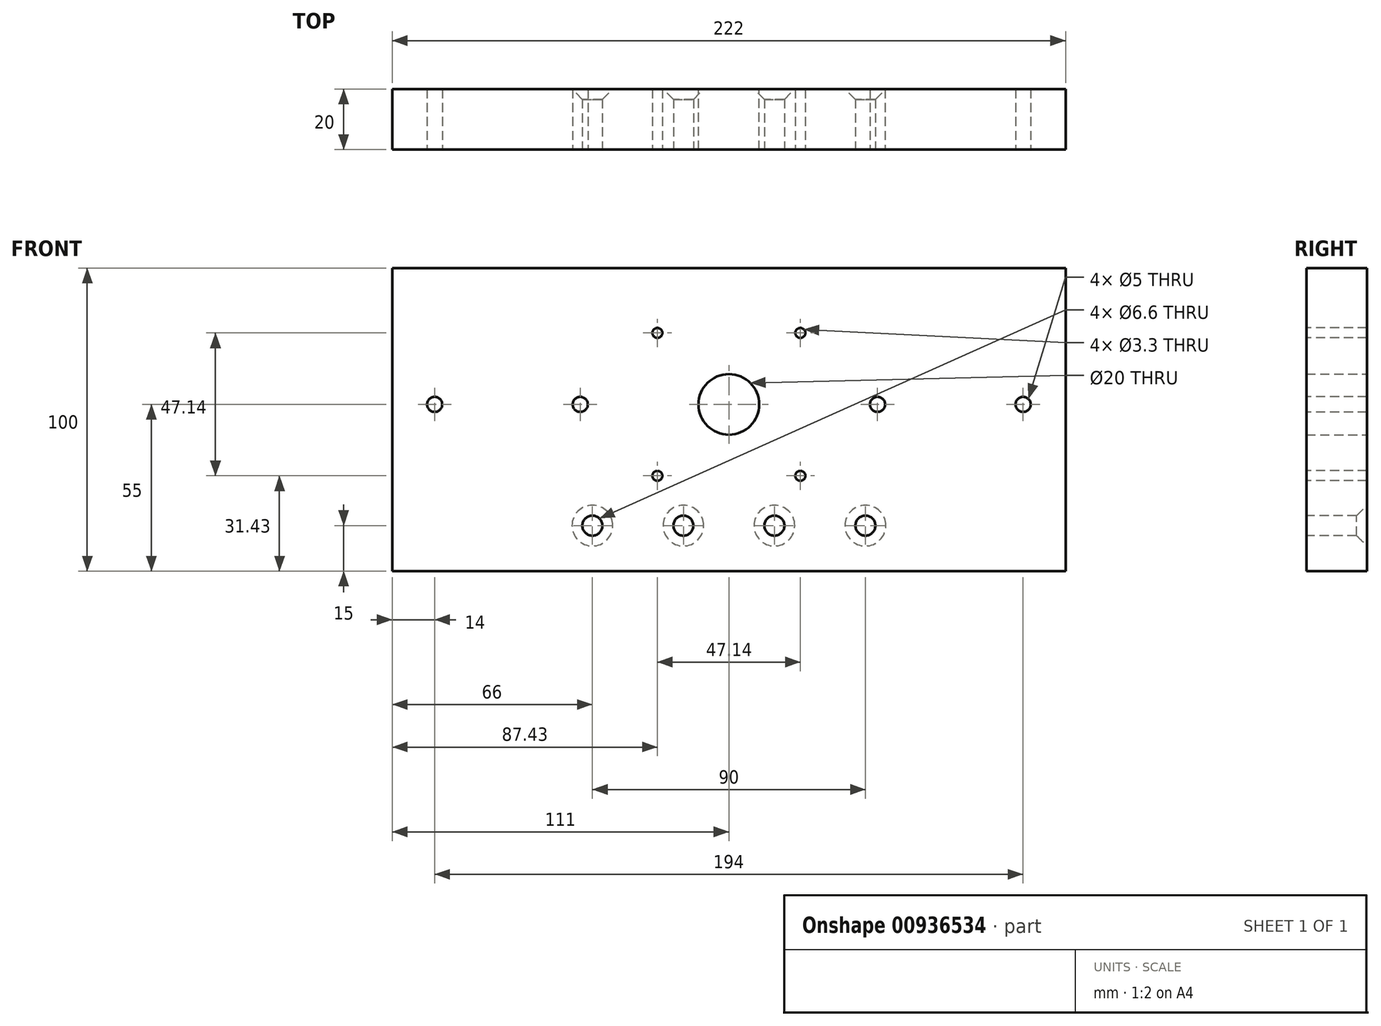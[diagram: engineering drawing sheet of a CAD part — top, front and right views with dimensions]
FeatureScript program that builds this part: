
annotation { "Feature Type Name" : "Feature", "Feature Type Description" : "" }
export const myFeature = defineFeature(function(context is Context, id is Id, definition is map)
    precondition{}
    {
        {
            var Q0;
            Q0=qCreatedBy(makeId("Front.planeOp"),FACE);
            var sketch = newSketch(context, id + "F0", { "sketchPlane" : qUnion([Q0])});
            skLineSegment(sketch, "E0.bottom", {"start": v(-111, -50) * mm, "end": v(111, -50) * mm});
            skLineSegment(sketch, "E0.top", {"start": v(-111, 50) * mm, "end": v(111, 50) * mm});
            skLineSegment(sketch, "E0.left", {"start": v(-111, -50) * mm, "end": v(-111, 50) * mm});
            skLineSegment(sketch, "E0.right", {"start": v(111, -50) * mm, "end": v(111, 50) * mm});
            skPoint(sketch, "E0.middle", {"position": v(0, 0) * mm});
            skLineSegment(sketch, "E1", {"start": v(-111, 5) * mm, "end": v(111, 5) * mm, "construction": true});
            skLineSegment(sketch, "E2", {"start": v(-73, 41.24) * mm, "end": v(-73, 0) * mm, "construction": true});
            skLineSegment(sketch, "E3.MirrorCS", {"start": v(73, 41.24) * mm, "end": v(73, 0) * mm, "construction": true});
            skLineSegment(sketch, "E4", {"start": v(-111, -20) * mm, "end": v(111, -20) * mm, "construction": true});
            skLineSegment(sketch, "E5", {"start": v(-97.11, -35) * mm, "end": v(93.84, -35) * mm, "construction": true});
            skPoint(sketch, "E6", {"position": v(-97, 5) * mm});
            skPoint(sketch, "E7.MirrorP", {"position": v(-49, 5) * mm});
            skPoint(sketch, "E8.MirrorP", {"position": v(49, 5) * mm});
            skPoint(sketch, "E9.MirrorP", {"position": v(97, 5) * mm});
            skPoint(sketch, "E10", {"position": v(-15, -35) * mm});
            skPoint(sketch, "E11", {"position": v(-45, -35) * mm});
            skPoint(sketch, "E12.MirrorP", {"position": v(15, -35) * mm});
            skPoint(sketch, "E13.MirrorP", {"position": v(45, -35) * mm});
            skCircle(sketch, "E14", {"center": v(0, 5) * mm, "radius": 10 * mm});
            skLineSegment(sketch, "E15.bottom", {"start": v(23.57, 28.57) * mm, "end": v(-23.57, 28.57) * mm, "construction": true});
            skLineSegment(sketch, "E15.top", {"start": v(23.57, -18.57) * mm, "end": v(-23.57, -18.57) * mm, "construction": true});
            skLineSegment(sketch, "E15.left", {"start": v(23.57, 28.57) * mm, "end": v(23.57, -18.57) * mm, "construction": true});
            skLineSegment(sketch, "E15.right", {"start": v(-23.57, 28.57) * mm, "end": v(-23.57, -18.57) * mm, "construction": true});
            skSolve(sketch);
        }
        {
            var Q0;
            Q0=makeQuery(id+"F0.imprint","IMPRINT",FACE,{"disambiguationData":[TD([[makeQuery(id+"F0.imprint","IMPRINT",EDGE,{"derivedFrom":sQuery(id+"F0.wireOp",EDGE,"E0.bottom")}),1.0]])]});
            extrude(context, id + "F1", {"entities" : qUnion([Q0]), "depth" : 20 * mm, "offsetDistance" : 25 * mm});
        }
        {
            var Q0;
            Q0=sQuery(id+"F0.wireOp",VERTEX,"E8.MirrorP");
            var Q1;
            Q1=sQuery(id+"F0.wireOp",VERTEX,"E9.MirrorP");
            var Q2;
            Q2=sQuery(id+"F0.wireOp",VERTEX,"E7.MirrorP");
            var Q3;
            Q3=sQuery(id+"F0.wireOp",VERTEX,"E6");
            var Q4;
            Q4=makeQuery(id+"F1.opExtrude","SWEPT_BODY",BODY,{"disambiguationData":[OSD([sQuery(id+"F0.wireOp",EDGE,"E0.bottom"),sQuery(id+"F0.wireOp",EDGE,"E0.top"),sQuery(id+"F0.wireOp",EDGE,"E0.left"),sQuery(id+"F0.wireOp",EDGE,"E0.right")])]});
            hole(context, id + "F2", {"style" : HoleStyle.SIMPLE, "endStyle" : HoleEndStyle.THROUGH, "oppositeDirection" : true, "standardTappedOrClearance" : lookupTablePath({ "standard" : "ISO", "engagement" : "75%", "pitch" : "1 mm", "size" : "M6", "type" : "Tapped" }), "standardBlindInLast" : lookupTablePath({ "standard" : "ISO", "engagement" : "75%", "pitch" : "1 mm", "size" : "M6", "type" : "Tapped" }), "holeDiameter" : 5 * mm, "majorDiameter" : 6 * mm, "showTappedDepth" : true, "tappedDepth" : 12 * mm, "tapClearance" : 3, "locations" : qUnion([Q0, Q1, Q2, Q3]), "scope" : qUnion([Q4]), "startStyle" : HoleStartStyle.PART});
        }
        {
            var Q0;
            Q0=sQuery(id+"F0.wireOp",VERTEX,"E11");
            var Q1;
            Q1=sQuery(id+"F0.wireOp",VERTEX,"E10");
            var Q2;
            Q2=sQuery(id+"F0.wireOp",VERTEX,"E12.MirrorP");
            var Q3;
            Q3=sQuery(id+"F0.wireOp",VERTEX,"E13.MirrorP");
            var Q4;
            Q4=makeQuery(id+"F1.opExtrude","SWEPT_BODY",BODY,{"disambiguationData":[OSD([sQuery(id+"F0.wireOp",EDGE,"E0.bottom"),sQuery(id+"F0.wireOp",EDGE,"E0.top"),sQuery(id+"F0.wireOp",EDGE,"E0.left"),sQuery(id+"F0.wireOp",EDGE,"E0.right")])]});
            hole(context, id + "F3", {"style" : HoleStyle.C_SINK, "endStyle" : HoleEndStyle.THROUGH, "oppositeDirection" : true, "standardTappedOrClearance" : lookupTablePath({ "fit" : "Normal", "standard" : "ISO", "size" : "M6", "type" : "Clearance" }), "standardBlindInLast" : lookupTablePath({ "fit" : "Standard", "standard" : "ISO", "size" : "M6", "type" : "Clearance" }), "holeDiameter" : 6.6 * mm, "cSinkDiameter" : 13.44 * mm, "cSinkAngle" : 90 * degree, "majorDiameter" : 6 * mm, "tappedDepth" : 12 * mm, "tapClearance" : 3, "locations" : qUnion([Q0, Q1, Q2, Q3]), "scope" : qUnion([Q4]), "startStyle" : HoleStartStyle.PART});
        }
        {
            var Q0;
            Q0=sQuery(id+"F0.wireOp",VERTEX,"E15.bottom.start");
            var Q1;
            Q1=sQuery(id+"F0.wireOp",VERTEX,"E15.bottom.end");
            var Q2;
            Q2=sQuery(id+"F0.wireOp",VERTEX,"E15.top.start");
            var Q3;
            Q3=sQuery(id+"F0.wireOp",VERTEX,"E15.top.end");
            var Q4;
            Q4=makeQuery(id+"F1.opExtrude","SWEPT_BODY",BODY,{"disambiguationData":[OSD([sQuery(id+"F0.wireOp",EDGE,"E0.bottom"),sQuery(id+"F0.wireOp",EDGE,"E0.top"),sQuery(id+"F0.wireOp",EDGE,"E0.left"),sQuery(id+"F0.wireOp",EDGE,"E0.right"),sQuery(id+"F0.wireOp",EDGE,"E14")])]});
            hole(context, id + "F4", {"style" : HoleStyle.SIMPLE, "endStyle" : HoleEndStyle.THROUGH, "oppositeDirection" : true, "standardTappedOrClearance" : lookupTablePath({ "standard" : "ISO", "engagement" : "75%", "pitch" : "0.7 mm", "size" : "M4", "type" : "Tapped" }), "standardBlindInLast" : lookupTablePath({ "standard" : "ISO", "engagement" : "75%", "pitch" : "0.7 mm", "size" : "M4", "type" : "Tapped" }), "holeDiameter" : 3.3 * mm, "majorDiameter" : 4 * mm, "showTappedDepth" : true, "tappedDepth" : 12 * mm, "tapClearance" : 3, "locations" : qUnion([Q0, Q1, Q2, Q3]), "scope" : qUnion([Q4]), "startStyle" : HoleStartStyle.PART});
        }
    });
